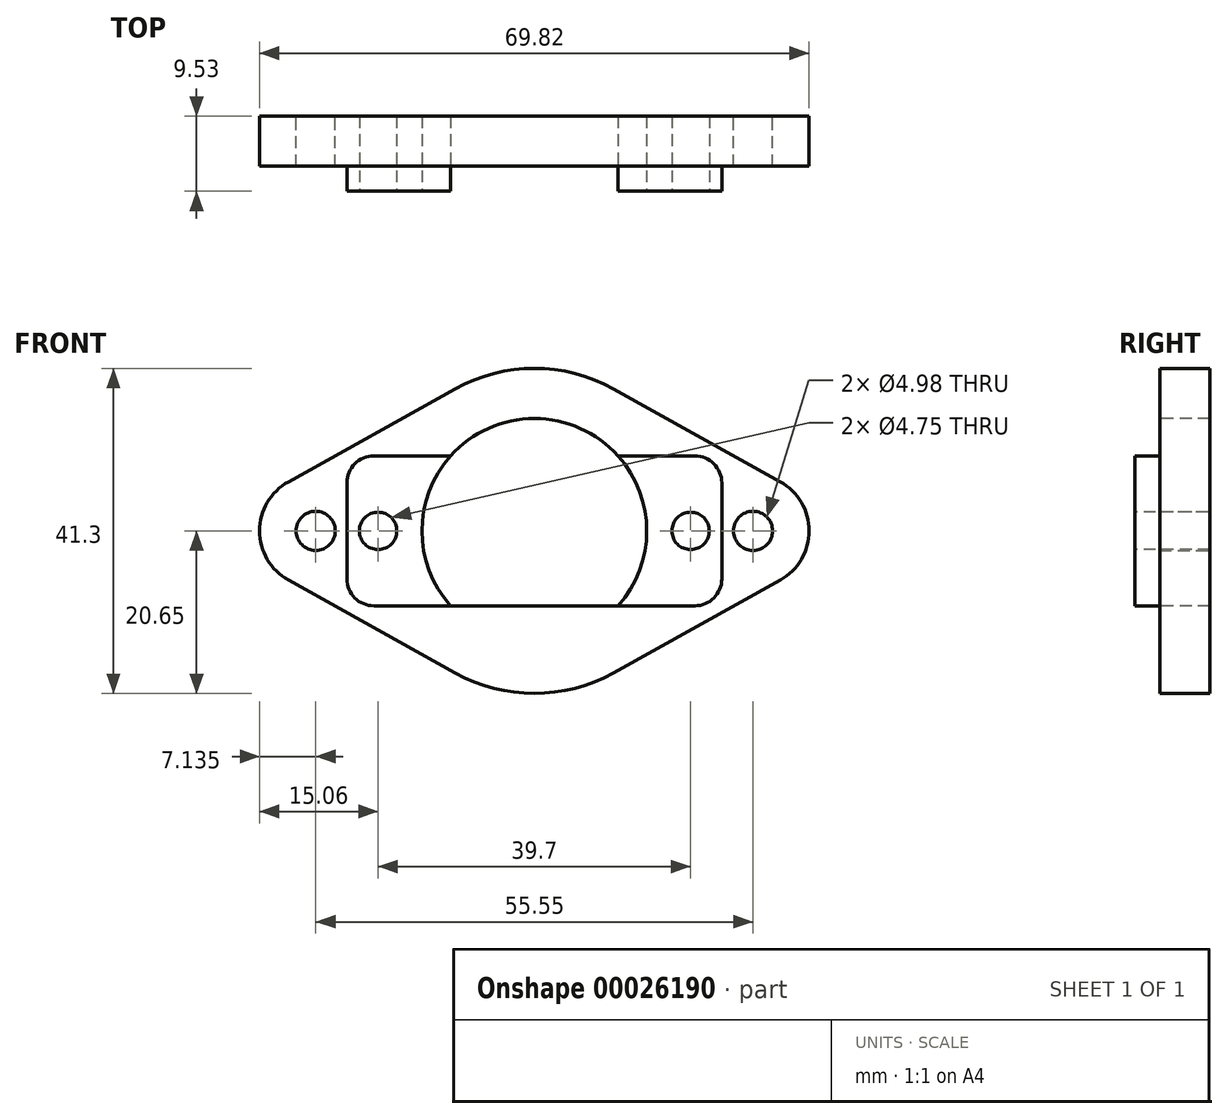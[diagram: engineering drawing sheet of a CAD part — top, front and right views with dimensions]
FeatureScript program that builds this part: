
annotation { "Feature Type Name" : "Feature", "Feature Type Description" : "" }
export const myFeature = defineFeature(function(context is Context, id is Id, definition is map)
    precondition{}
    {
        {
            var Q0;
            Q0=qCreatedBy(makeId("Front.planeOp"),FACE);
            var sketch = newSketch(context, id + "F0", { "sketchPlane" : qUnion([Q0])});
            skArc(sketch, "E0", {"start": v(-20.65, 0.37) * mm, "mid": v(-20.65, 0) * mm, "end": v(-20.65, -0.37) * mm});
            skArc(sketch, "E1", {"start": v(20.65, 0.37) * mm, "mid": v(20.64, 0) * mm, "end": v(20.65, -0.37) * mm});
            skArc(sketch, "E2", {"start": v(-31.25, 6.24) * mm, "mid": v(-34.91, 0) * mm, "end": v(-31.25, -6.24) * mm});
            skCircle(sketch, "E3", {"center": v(-27.77, 0) * mm, "radius": 2.49 * mm});
            skCircle(sketch, "E4", {"center": v(27.77, 0) * mm, "radius": 2.49 * mm});
            skLineSegment(sketch, "E5", {"start": v(0, 38.42) * mm, "end": v(0, -46.4) * mm, "construction": true});
            skLineSegment(sketch, "E6", {"start": v(-10.05, 18.04) * mm, "end": v(-31.25, 6.24) * mm});
            skLineSegment(sketch, "E7", {"start": v(-31.25, -6.24) * mm, "end": v(-10.05, -18.04) * mm});
            skLineSegment(sketch, "E8", {"start": v(10.05, -18.04) * mm, "end": v(31.25, -6.24) * mm});
            skLineSegment(sketch, "E9", {"start": v(31.25, 6.24) * mm, "end": v(10.05, 18.04) * mm});
            skArc(sketch, "E10.trimOffspring", {"start": v(-20.65, -0.37) * mm, "mid": v(-20.64, 0) * mm, "end": v(-20.65, 0.37) * mm});
            skArc(sketch, "E11.trimOffspring", {"start": v(-10.05, -18.04) * mm, "mid": v(0, -20.65) * mm, "end": v(10.05, -18.04) * mm});
            skArc(sketch, "E12.trimOffspring", {"start": v(10.05, 18.04) * mm, "mid": v(0, 20.65) * mm, "end": v(-10.05, 18.04) * mm});
            skArc(sketch, "E13.trimOffspring", {"start": v(31.25, -6.24) * mm, "mid": v(34.91, 0) * mm, "end": v(31.25, 6.24) * mm});
            skArc(sketch, "E14.trimOffspring", {"start": v(20.65, -0.37) * mm, "mid": v(20.65, 0) * mm, "end": v(20.65, 0.37) * mm});
            skSolve(sketch);
        }
        {
            var Q0;
            Q0=makeQuery(id+"F0.imprint","IMPRINT",FACE,{"disambiguationData":[TD([[makeQuery(id+"F0.imprint","IMPRINT",EDGE,{"derivedFrom":sQuery(id+"F0.wireOp",EDGE,"E0")}),-1.0]])]});
            extrude(context, id + "F1", {"entities" : qUnion([Q0]), "depth" : 6.35 * mm});
        }
        {
            var Q0;
            Q0=makeQuery(id+"F1.opExtrude","CAP_FACE",FACE,{"disambiguationData":[OSD([sQuery(id+"F0.wireOp",EDGE,"E0"),sQuery(id+"F0.wireOp",EDGE,"E1"),sQuery(id+"F0.wireOp",EDGE,"E2"),sQuery(id+"F0.wireOp",EDGE,"E3"),sQuery(id+"F0.wireOp",EDGE,"E4"),sQuery(id+"F0.wireOp",EDGE,"E6"),sQuery(id+"F0.wireOp",EDGE,"E7"),sQuery(id+"F0.wireOp",EDGE,"E8"),sQuery(id+"F0.wireOp",EDGE,"E9"),sQuery(id+"F0.wireOp",EDGE,"E10.trimOffspring"),sQuery(id+"F0.wireOp",EDGE,"E11.trimOffspring"),sQuery(id+"F0.wireOp",EDGE,"E12.trimOffspring"),sQuery(id+"F0.wireOp",EDGE,"E13.trimOffspring"),sQuery(id+"F0.wireOp",EDGE,"E14.trimOffspring")])],"isStart":false});
            var sketch = newSketch(context, id + "F2", { "sketchPlane" : qUnion([Q0])});
            skLineSegment(sketch, "E15.rect.bottom", {"start": v(23.81, -9.52) * mm, "end": v(-23.81, -9.53) * mm});
            skLineSegment(sketch, "E15.rect.top", {"start": v(23.81, 9.53) * mm, "end": v(-23.81, 9.52) * mm});
            skLineSegment(sketch, "E15.rect.left", {"start": v(23.81, -9.52) * mm, "end": v(23.81, 9.53) * mm});
            skLineSegment(sketch, "E15.rect.right", {"start": v(-23.81, -9.53) * mm, "end": v(-23.81, 9.52) * mm});
            skPoint(sketch, "E15.rect.middle", {"position": v(0, 0) * mm});
            skSolve(sketch);
        }
        {
            var Q0;
            Q0=makeQuery(id+"F2.imprint","IMPRINT",FACE,{"disambiguationData":[TD([[makeQuery(id+"F2.imprint","IMPRINT",EDGE,{"derivedFrom":sQuery(id+"F2.wireOp",EDGE,"E15.rect.bottom")}),-1.0]])]});
            extrude(context, id + "F3", {"entities" : qUnion([Q0]), "operationType" : NewBodyOperationType.ADD, "depth" : 3.17 * mm});
        }
        {
            var Q0;
            Q0=makeQuery(id+"F3.opExtrude","SWEPT_EDGE",EDGE,{"disambiguationData":[OSD([sQuery(id+"F2.wireOp",EDGE,"E15.rect.top"),sQuery(id+"F2.wireOp",EDGE,"E15.rect.right")])]});
            var Q1;
            Q1=makeQuery(id+"F3.opExtrude","SWEPT_EDGE",EDGE,{"disambiguationData":[OSD([sQuery(id+"F2.wireOp",EDGE,"E15.rect.bottom"),sQuery(id+"F2.wireOp",EDGE,"E15.rect.right")])]});
            var Q2;
            Q2=makeQuery(id+"F3.opExtrude","SWEPT_EDGE",EDGE,{"disambiguationData":[OSD([sQuery(id+"F2.wireOp",EDGE,"E15.rect.top"),sQuery(id+"F2.wireOp",EDGE,"E15.rect.left")])]});
            var Q3;
            Q3=makeQuery(id+"F3.opExtrude","SWEPT_EDGE",EDGE,{"disambiguationData":[OSD([sQuery(id+"F2.wireOp",EDGE,"E15.rect.bottom"),sQuery(id+"F2.wireOp",EDGE,"E15.rect.left")])]});
            fillet(context, id + "F4", {"entities" : qUnion([Q0, Q1, Q2, Q3]), "radius" : 3.43 * mm, "tangentPropagation" : true, "allowEdgeOverflow" : false});
        }
        {
            var Q0;
            Q0=makeQuery(id+"F3.opExtrude","CAP_FACE",FACE,{"disambiguationData":[OSD([sQuery(id+"F0.wireOp",EDGE,"E0"),sQuery(id+"F0.wireOp",EDGE,"E1"),sQuery(id+"F0.wireOp",EDGE,"E10.trimOffspring"),sQuery(id+"F0.wireOp",EDGE,"E14.trimOffspring"),sQuery(id+"F2.wireOp",EDGE,"E15.rect.bottom"),sQuery(id+"F2.wireOp",EDGE,"E15.rect.top"),sQuery(id+"F2.wireOp",EDGE,"E15.rect.left"),sQuery(id+"F2.wireOp",EDGE,"E15.rect.right")])],"isStart":false});
            var sketch = newSketch(context, id + "F5", { "sketchPlane" : qUnion([Q0])});
            skCircle(sketch, "E16", {"center": v(0, 0) * mm, "radius": 14.27 * mm});
            skCircle(sketch, "E17", {"center": v(-19.85, 0) * mm, "radius": 2.37 * mm});
            skCircle(sketch, "E18", {"center": v(19.85, 0) * mm, "radius": 2.37 * mm});
            skLineSegment(sketch, "E19", {"start": v(0, 19.54) * mm, "end": v(0, -18.4) * mm, "construction": true});
            skSolve(sketch);
        }
        {
            var Q0;
            Q0=makeQuery(id+"F5.imprint","IMPRINT",FACE,{"disambiguationData":[TD([[makeQuery(id+"F5.imprint","IMPRINT",EDGE,{"derivedFrom":sQuery(id+"F5.wireOp",EDGE,"E17")}),1.0]])]});
            var Q1;
            {var subQ0=makeQuery(id+"F3.opExtrude","CAP_EDGE",EDGE,{"disambiguationData":[OSD([sQuery(id+"F2.wireOp",EDGE,"E15.rect.top")])],"isStart":false});var subQ1=sQuery(id+"F5.wireOp",EDGE,"E16");var subQ3=makeQuery(id+"F5.imprint","INTERSECT",VERTEX,{"disambiguationData":[OD(0.0)],"derivedFrom":[subQ0,subQ1]});Q1=makeQuery(id+"F5.imprint","IMPRINT",FACE,{"disambiguationData":[TD([[makeQuery(id+"F5.imprint","IMPRINT",EDGE,{"disambiguationData":[TD([[subQ3,-1.0]])],"derivedFrom":subQ1}),1.0]])]});}
            var Q2;
            {var subQ0=makeQuery(id+"F3.opExtrude","CAP_EDGE",EDGE,{"disambiguationData":[OSD([sQuery(id+"F2.wireOp",EDGE,"E15.rect.top")])],"isStart":false});var subQ1=sQuery(id+"F5.wireOp",EDGE,"E16");var subQ3=makeQuery(id+"F5.imprint","INTERSECT",VERTEX,{"disambiguationData":[OD(0.0)],"derivedFrom":[subQ0,subQ1]});Q2=makeQuery(id+"F5.imprint","IMPRINT",FACE,{"disambiguationData":[TD([[makeQuery(id+"F5.imprint","IMPRINT",EDGE,{"disambiguationData":[TD([[subQ3,1.0]])],"derivedFrom":subQ1}),1.0]])]});}
            var Q3;
            {var subQ0=makeQuery(id+"F3.opExtrude","CAP_EDGE",EDGE,{"disambiguationData":[OSD([sQuery(id+"F2.wireOp",EDGE,"E15.rect.bottom")])],"isStart":false});var subQ1=sQuery(id+"F5.wireOp",EDGE,"E16");var subQ3=makeQuery(id+"F5.imprint","INTERSECT",VERTEX,{"disambiguationData":[OD(0.0)],"derivedFrom":[subQ0,subQ1]});Q3=makeQuery(id+"F5.imprint","IMPRINT",FACE,{"disambiguationData":[TD([[makeQuery(id+"F5.imprint","IMPRINT",EDGE,{"disambiguationData":[TD([[subQ3,-1.0]])],"derivedFrom":subQ1}),1.0]])]});}
            var Q4;
            Q4=makeQuery(id+"F5.imprint","IMPRINT",FACE,{"disambiguationData":[TD([[makeQuery(id+"F5.imprint","IMPRINT",EDGE,{"derivedFrom":sQuery(id+"F5.wireOp",EDGE,"E18")}),1.0]])]});
            extrude(context, id + "F6", {"entities" : qUnion([Q0, Q1, Q2, Q3, Q4]), "operationType" : NewBodyOperationType.REMOVE, "endBound" : BoundingType.THROUGH_ALL, "oppositeDirection" : true, "depth" : 25.4 * mm});
        }
    });
